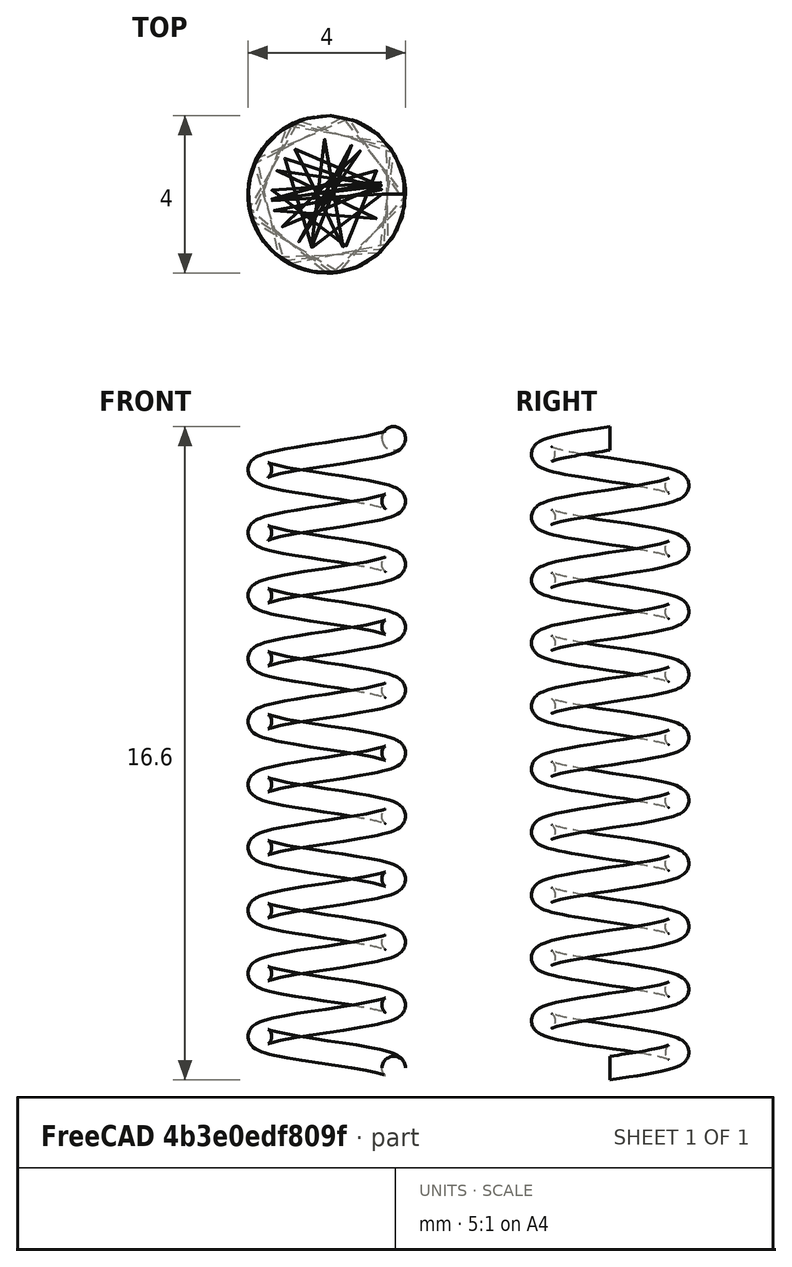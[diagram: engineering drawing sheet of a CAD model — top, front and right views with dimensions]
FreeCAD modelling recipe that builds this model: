
FCSTD DOCUMENT  (FreeCAD 0.14R3702 (Git))
Label: Extruder-spring
License: CC-BY 3.0
LicenseURL: http://creativecommons.org/licenses/by/3.0/
objects: Part::Helix×1, Sketcher::SketchObject×1, Part::Sweep×1, Part::Feature×1
note: 4 computed .brp shape members not serialized (recipe doc carries the construction recipe); baked Part::Feature solids carry a one-line shape summary decoded from their .brp

FEATURE [Part::Helix] Helix
  Angle = 0
  Height = 16
  LocalCoord = 0
  Pitch = 1.6
  Radius = 1.7
  Style = 1
FEATURE [Sketcher::SketchObject] Sketch  label="spring-section"
  Placement = pos=(0,0,0) rot=(1,0,0;1.5708rad)
  sketch-geometry (1):
    g0: Circle CenterX=1.7 CenterY=0 CenterZ=0 NormalX=0 NormalY=0 NormalZ=1 Radius=0.3
  constraints (3):
    c: PointOnObject(g0,g-1)
    c: Radius(g0) = 0.3
    c: DistanceX(g-1,g0) = 1.7
FEATURE [Part::Sweep] Sweep  label="spring"
  Frenet = true
  Sections = -> [Sketch]
  Solid = true
  Spine = -> Helix [Edge1]
  Transition = 1
FEATURE [Part::Feature] Sweep001  label="Extruder-spring-final"
  shape: bbox 5.171 x 5.171 x 17.14 mm, 3 faces (baked)
